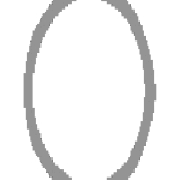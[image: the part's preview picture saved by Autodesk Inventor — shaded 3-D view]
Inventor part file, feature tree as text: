
AUTODESK INVENTOR PART (.ipt)
format: ipt  version: 2021 (Build 250183000, 183)  size: 141,824 bytes
history: native  units: in
note: dims shown in document units (in); Inventor stores cm internally (conversion verified against a paired STEP export)
features: other x5, sketch x2, sweep x1, plane x1
ambient origin geometry x8: Origin, YZ Plane, XZ Plane, XY Plane, X Axis, Y Axis, Z Axis, Center Point
bodies: Solid1 (feature_tree), Body (feature_tree)
feature tree (9):
  other  "Driven Length"
  other  "Frame Generator"
  other  "Start Plane"
  other  "End Plane"
  sweep  "Sweep Path"
  other  "Orientation Work Plane"
  sketch  "Sketch2"  dims[d0=1.0in d1=0.065in]
  plane  "Work Plane3"
  sketch  "Sketch3"  dims[d2=1.1738in d4=-0.0in d5=1.1738in d8=90.0deg d9=1.1738in d10=0.0in d11=0.0in]
